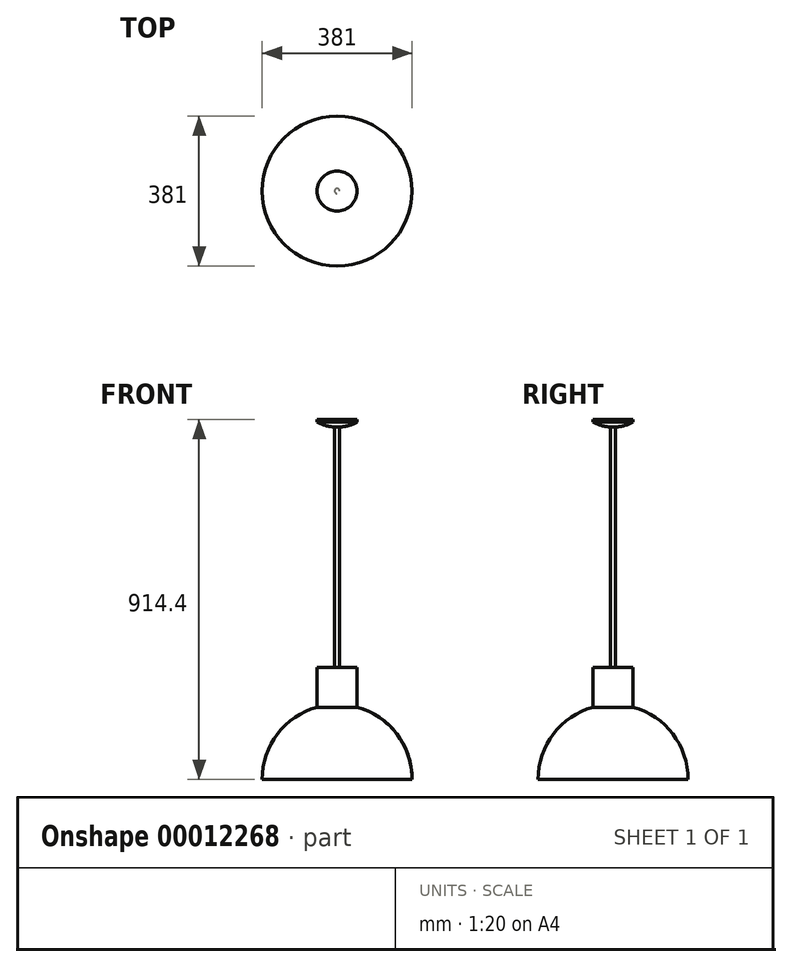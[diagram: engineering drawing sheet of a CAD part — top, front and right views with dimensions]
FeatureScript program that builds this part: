
annotation { "Feature Type Name" : "Feature", "Feature Type Description" : "" }
export const myFeature = defineFeature(function(context is Context, id is Id, definition is map)
    precondition{}
    {
        {
            var Q0;
            Q0=qCreatedBy(makeId("Front.planeOp"),FACE);
            var sketch = newSketch(context, id + "F0", { "sketchPlane" : qUnion([Q0])});
            skLineSegment(sketch, "E0", {"start": v(0, 0) * mm, "end": v(0, -121.5) * mm, "construction": true});
            skLineSegment(sketch, "E1", {"start": v(-190.5, 0) * mm, "end": v(0, 0) * mm});
            skLineSegment(sketch, "E2", {"start": v(0, 914.4) * mm, "end": v(-50.8, 914.4) * mm});
            skLineSegment(sketch, "E3", {"start": v(0, 0) * mm, "end": v(0, 914.4) * mm});
            skLineSegment(sketch, "E4", {"start": v(-50.8, 914.4) * mm, "end": v(-50.8, 908.05) * mm});
            skArc(sketch, "E5", {"start": v(-50.8, 183.6) * mm, "mid": v(-151.6, 115.35) * mm, "end": v(-190.5, 0) * mm});
            skLineSegment(sketch, "E6", {"start": v(-50.8, 183.6) * mm, "end": v(-50.8, 285.2) * mm});
            skLineSegment(sketch, "E7", {"start": v(-50.8, 285.2) * mm, "end": v(-6.35, 285.2) * mm});
            skLineSegment(sketch, "E8", {"start": v(-6.35, 285.2) * mm, "end": v(-6.35, 895.35) * mm});
            skArc(sketch, "E9", {"start": v(-50.8, 908.05) * mm, "mid": v(-29.27, 899.26) * mm, "end": v(-6.35, 895.35) * mm});
            skSolve(sketch);
        }
        {
            var Q0;
            Q0 = qSketchRegion(id + "F0", true);
            var Q1;
            Q1=sQuery(id+"F0.wireOp",EDGE,"E0");
            revolve(context, id + "F1", {"entities" : qUnion([Q0]), "axis" : qUnion([Q1]), "revolveType" : RevolveType.FULL});
        }
    });
